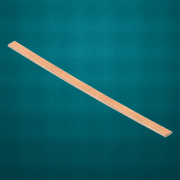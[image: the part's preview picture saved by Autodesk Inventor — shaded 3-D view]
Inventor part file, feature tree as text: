
AUTODESK INVENTOR PART (.ipt)
format: ipt  version: 2017 (Build 210142000, 142)  size: 142,848 bytes
history: native  units: in
note: dims shown in document units (in); Inventor stores cm internally (conversion verified against a paired STEP export)
features: sketch x2, extrude x1, fillet x1, other x1
ambient origin geometry x8: Origin, YZ Plane, XZ Plane, XY Plane, X Axis, Y Axis, Z Axis, Center Point
bodies: Solid1 (feature_tree)
feature tree (5):
  extrude  "Extrusion1"  Depth=1.375in
  fillet  "Fillet1"  Radius=30.0in
  other  "Bend Part1"
  sketch  "Sketch1"  dims[d0=1.375in d1=0.375in d2=30.0in d3=0.0in]
  sketch  "Sketch2"  dims[d4=0.125in d5=346.0in d6=0.0344in]
